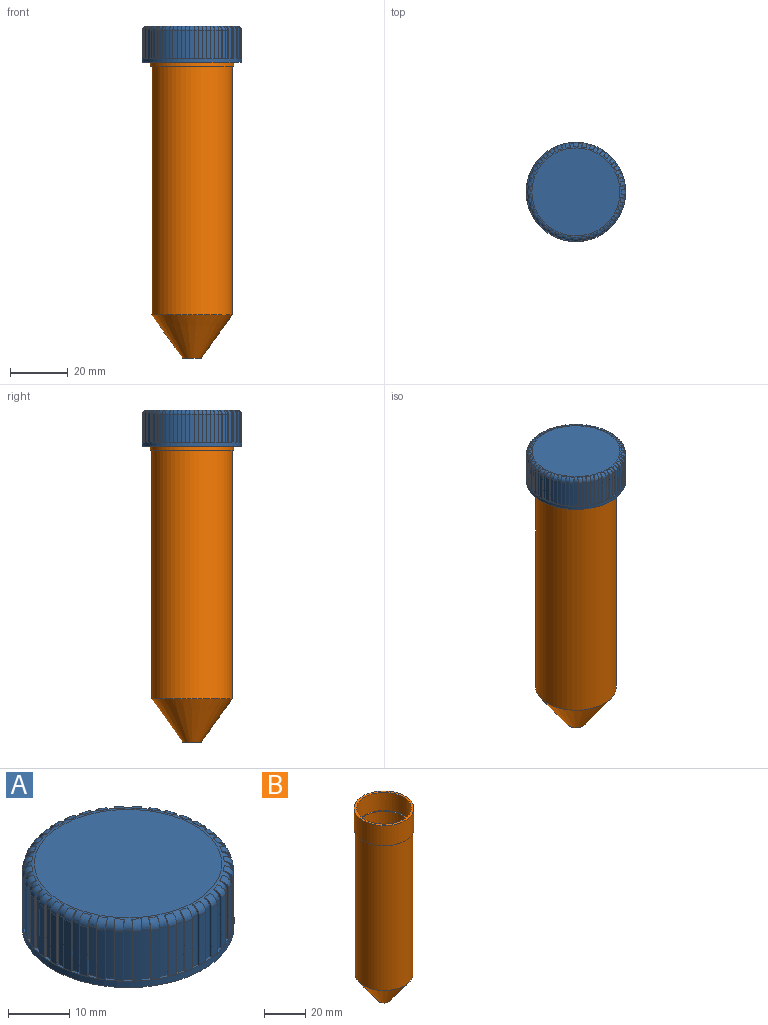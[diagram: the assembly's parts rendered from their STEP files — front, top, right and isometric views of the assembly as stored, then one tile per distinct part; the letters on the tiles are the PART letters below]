
ASSEMBLY  parts=2 mates=1
PART A: 223 faces, bbox 36.3x36.3x12.5 mm
  f0: cylinder r=16.75mm len=9.75mm, axis (0,0,1), area 13.9mm2, adj f37,f42,f179,f184
  f1: cylinder r=16.75mm len=9.75mm, axis (0,0,1), area 13.9mm2, adj f37,f42,f175,f180
  f2: cylinder r=16.75mm len=9.75mm, axis (0,0,1), area 13.9mm2, adj f37,f42,f171,f176
  f3: cylinder r=16.75mm len=9.75mm, axis (0,0,1), area 13.9mm2, adj f37,f42,f167,f172
  f4: cylinder r=16.75mm len=9.75mm, axis (0,0,1), area 13.9mm2, adj f37,f42,f163,f168
  f5: cylinder r=16.75mm len=9.75mm, axis (0,0,1), area 13.9mm2, adj f37,f42,f159,f164
  f6: cylinder r=16.75mm len=9.75mm, axis (0,0,1), area 13.9mm2, adj f37,f42,f155,f160
  f7: cylinder r=16.75mm len=9.75mm, axis (0,0,1), area 13.9mm2, adj f37,f42,f151,f156
  f8: cylinder r=16.75mm len=9.75mm, axis (0,0,1), area 13.9mm2, adj f37,f42,f147,f152
  f9: cylinder r=16.75mm len=9.75mm, axis (0,0,1), area 13.9mm2, adj f37,f42,f143,f148
  f10: cylinder r=16.75mm len=9.75mm, axis (0,0,1), area 13.9mm2, adj f37,f42,f139,f144
  f11: cylinder r=16.75mm len=9.75mm, axis (0,0,1), area 13.9mm2, adj f37,f42,f135,f140
  f12: cylinder r=16.75mm len=9.75mm, axis (0,0,1), area 13.9mm2, adj f37,f42,f131,f136
  f13: cylinder r=16.75mm len=9.75mm, axis (0,0,1), area 13.9mm2, adj f37,f42,f127,f132
  f14: cylinder r=16.75mm len=9.75mm, axis (0,0,1), area 13.9mm2, adj f37,f42,f123,f128
  f15: cylinder r=16.75mm len=9.75mm, axis (0,0,1), area 13.9mm2, adj f37,f42,f119,f124
  f16: cylinder r=16.75mm len=9.75mm, axis (0,0,1), area 13.9mm2, adj f37,f42,f115,f120
  f17: cylinder r=16.75mm len=9.75mm, axis (0,0,1), area 13.9mm2, adj f37,f42,f111,f116
  f18: cylinder r=16.75mm len=9.75mm, axis (0,0,1), area 13.9mm2, adj f37,f42,f107,f112
  f19: cylinder r=16.75mm len=9.75mm, axis (0,0,1), area 13.9mm2, adj f37,f42,f103,f108
  f20: cylinder r=16.75mm len=9.75mm, axis (0,0,1), area 13.9mm2, adj f37,f42,f99,f104
  f21: cylinder r=16.75mm len=9.75mm, axis (0,0,1), area 13.9mm2, adj f37,f42,f95,f100
  f22: cylinder r=16.75mm len=9.75mm, axis (0,0,1), area 13.9mm2, adj f37,f42,f91,f96
  f23: cylinder r=16.75mm len=9.75mm, axis (0,0,1), area 13.9mm2, adj f37,f42,f87,f92
  f24: cylinder r=16.75mm len=9.75mm, axis (0,0,1), area 13.9mm2, adj f37,f42,f83,f88
  f25: cylinder r=16.75mm len=9.75mm, axis (0,0,1), area 13.9mm2, adj f37,f42,f79,f84
  f26: cylinder r=16.75mm len=9.75mm, axis (0,0,1), area 13.9mm2, adj f37,f42,f75,f80
  f27: cylinder r=16.75mm len=9.75mm, axis (0,0,1), area 13.9mm2, adj f37,f42,f71,f76
  f28: cylinder r=16.75mm len=9.75mm, axis (0,0,1), area 13.9mm2, adj f37,f42,f67,f72
  f29: cylinder r=16.75mm len=9.75mm, axis (0,0,1), area 13.9mm2, adj f37,f42,f63,f68
  f30: cylinder r=16.75mm len=9.75mm, axis (0,0,1), area 13.9mm2, adj f37,f42,f59,f64
  f31: cylinder r=16.75mm len=9.75mm, axis (0,0,1), area 13.9mm2, adj f37,f42,f55,f60
  f32: cylinder r=16.75mm len=9.75mm, axis (0,0,1), area 13.9mm2, adj f37,f42,f51,f56
  f33: cylinder r=16.75mm len=9.75mm, axis (0,0,1), area 13.9mm2, adj f37,f42,f47,f52
  f34: cylinder r=16.75mm len=9.75mm, axis (0,0,1), area 13.9mm2, adj f37,f42,f43,f48
  f35: plane 30.5x30.5mm, normal (0,0,1), area 730.6mm2, adj f42
  f36: cylinder r=16.75mm len=9.75mm, axis (0,0,1), area 13.9mm2, adj f37,f42,f44,f183
  f37: plane 34.5x34.5mm, normal (0,0,1), area 31.5mm2, adj f0,f1,f2,f3,f4,f5,f6,f7
  f38: cylinder r=17.25mm len=34.5mm, axis (0,0,1), area 135.5mm2, adj f37,f39
  f39: plane 34.5x34.5mm, normal (0,0,-1), area 175.2mm2, adj f38,f40
  f40: cylinder r=15.55mm len=31.1mm, axis (0,0,1), area 1025.9mm2, adj f39,f41
  f41: plane 31.1x31.1mm, normal (0,0,-1), area 759.6mm2, adj f40
  f42: torus R=15.25mm, axis (0,0,-1), area 134.8mm2, adj f0,f1,f2,f3,f4,f5,f6,f7
  f43: plane 11.25x1.5mm, normal (0,1,0), area 4.7mm2, adj f34,f37,f42,f45,f46,f222
  f44: plane 11.25x1.5mm, normal (0,-1,0), area 4.7mm2, adj f36,f37,f42,f45,f46,f222
  f45: plane 9.75x1.5mm, normal (-1,0,0), area 14.6mm2, adj f37,f43,f44,f222
  f46: plane 1.51x0.07mm, normal (1,0,0), area 0.1mm2, adj f42,f43,f44,f222
  f47: plane 11.25x1.48mm, normal (0.17,0.98,0), area 4.7mm2, adj f33,f37,f42,f49,f50,f221
  f48: plane 11.25x1.48mm, normal (-0.17,-0.98,0), area 4.7mm2, adj f34,f37,f42,f49,f50,f221
  f49: plane 9.75x1.48mm, normal (-0.98,0.17,0), area 14.6mm2, adj f37,f47,f48,f221
  f50: plane 1.48x0.26mm, normal (0.98,-0.17,0), area 0.1mm2, adj f42,f47,f48,f221
  f51: plane 11.25x1.41mm, normal (0.34,0.94,0), area 4.7mm2, adj f32,f37,f42,f53,f54,f220
  f52: plane 11.25x1.41mm, normal (-0.34,-0.94,0), area 4.7mm2, adj f33,f37,f42,f53,f54,f220
  f53: plane 9.75x1.41mm, normal (-0.94,0.34,0), area 14.6mm2, adj f37,f51,f52,f220
  f54: plane 1.41x0.51mm, normal (0.94,-0.34,0), area 0.1mm2, adj f42,f51,f52,f220
  f55: plane 11.25x1.3mm, normal (0.5,0.87,0), area 4.7mm2, adj f31,f37,f42,f57,f58,f219
  f56: plane 11.25x1.3mm, normal (-0.5,-0.87,0), area 4.7mm2, adj f32,f37,f42,f57,f58,f219
  f57: plane 9.75x1.3mm, normal (-0.87,0.5,0), area 14.6mm2, adj f37,f55,f56,f219
  f58: plane 1.3x0.75mm, normal (0.87,-0.5,0), area 0.1mm2, adj f42,f55,f56,f219
  f59: plane 11.25x1.15mm, normal (0.64,0.77,0), area 4.7mm2, adj f30,f37,f42,f61,f62,f218
  f60: plane 11.25x1.15mm, normal (-0.64,-0.77,0), area 4.7mm2, adj f31,f37,f42,f61,f62,f218
  f61: plane 9.75x1.15mm, normal (-0.77,0.64,0), area 14.6mm2, adj f37,f59,f60,f218
  f62: plane 1.15x0.96mm, normal (0.77,-0.64,0), area 0.1mm2, adj f42,f59,f60,f218
  f63: plane 11.25x1.15mm, normal (0.77,0.64,0), area 4.7mm2, adj f29,f37,f42,f65,f66,f217
  f64: plane 11.25x1.15mm, normal (-0.77,-0.64,0), area 4.7mm2, adj f30,f37,f42,f65,f66,f217
  f65: plane 9.75x1.15mm, normal (-0.64,0.77,0), area 14.6mm2, adj f37,f63,f64,f217
  f66: plane 1.15x0.96mm, normal (0.64,-0.77,0), area 0.1mm2, adj f42,f63,f64,f217
  f67: plane 11.25x1.3mm, normal (0.87,0.5,0), area 4.7mm2, adj f28,f37,f42,f69,f70,f216
  f68: plane 11.25x1.3mm, normal (-0.87,-0.5,0), area 4.7mm2, adj f29,f37,f42,f69,f70,f216
  f69: plane 9.75x1.3mm, normal (-0.5,0.87,0), area 14.6mm2, adj f37,f67,f68,f216
  f70: plane 1.3x0.75mm, normal (0.5,-0.87,0), area 0.1mm2, adj f42,f67,f68,f216
  f71: plane 11.25x1.41mm, normal (0.94,0.34,0), area 4.7mm2, adj f27,f37,f42,f73,f74,f215
  f72: plane 11.25x1.41mm, normal (-0.94,-0.34,0), area 4.7mm2, adj f28,f37,f42,f73,f74,f215
  f73: plane 9.75x1.41mm, normal (-0.34,0.94,0), area 14.6mm2, adj f37,f71,f72,f215
  f74: plane 1.41x0.51mm, normal (0.34,-0.94,0), area 0.1mm2, adj f42,f71,f72,f215
  f75: plane 11.25x1.48mm, normal (0.98,0.17,0), area 4.7mm2, adj f26,f37,f42,f77,f78,f214
  f76: plane 11.25x1.48mm, normal (-0.98,-0.17,0), area 4.7mm2, adj f27,f37,f42,f77,f78,f214
  f77: plane 9.75x1.48mm, normal (-0.17,0.98,0), area 14.6mm2, adj f37,f75,f76,f214
  f78: plane 1.48x0.26mm, normal (0.17,-0.98,0), area 0.1mm2, adj f42,f75,f76,f214
  f79: plane 11.25x1.5mm, normal (1,0,0), area 4.7mm2, adj f25,f37,f42,f81,f82,f213
  f80: plane 11.25x1.5mm, normal (-1,0,0), area 4.7mm2, adj f26,f37,f42,f81,f82,f213
  f81: plane 9.75x1.5mm, normal (0,1,0), area 14.6mm2, adj f37,f79,f80,f213
  f82: plane 1.5x0.06mm, normal (0,-1,0), area 0.1mm2, adj f42,f79,f80,f213
  f83: plane 11.25x1.48mm, normal (0.98,-0.17,0), area 4.7mm2, adj f24,f37,f42,f85,f86,f212
  f84: plane 11.25x1.48mm, normal (-0.98,0.17,0), area 4.7mm2, adj f25,f37,f42,f85,f86,f212
  f85: plane 9.75x1.48mm, normal (0.17,0.98,0), area 14.6mm2, adj f37,f83,f84,f212
  f86: plane 1.48x0.26mm, normal (-0.17,-0.98,0), area 0.1mm2, adj f42,f83,f84,f212
  f87: plane 11.25x1.41mm, normal (0.94,-0.34,0), area 4.7mm2, adj f23,f37,f42,f89,f90,f211
  f88: plane 11.25x1.41mm, normal (-0.94,0.34,0), area 4.7mm2, adj f24,f37,f42,f89,f90,f211
  f89: plane 9.75x1.41mm, normal (0.34,0.94,0), area 14.6mm2, adj f37,f87,f88,f211
  f90: plane 1.41x0.51mm, normal (-0.34,-0.94,0), area 0.1mm2, adj f42,f87,f88,f211
  f91: plane 11.25x1.3mm, normal (0.87,-0.5,0), area 4.7mm2, adj f22,f37,f42,f93,f94,f210
  f92: plane 11.25x1.3mm, normal (-0.87,0.5,0), area 4.7mm2, adj f23,f37,f42,f93,f94,f210
  f93: plane 9.75x1.3mm, normal (0.5,0.87,0), area 14.6mm2, adj f37,f91,f92,f210
  f94: plane 1.3x0.75mm, normal (-0.5,-0.87,0), area 0.1mm2, adj f42,f91,f92,f210
  f95: plane 11.25x1.15mm, normal (0.77,-0.64,0), area 4.7mm2, adj f21,f37,f42,f97,f98,f209
  f96: plane 11.25x1.15mm, normal (-0.77,0.64,0), area 4.7mm2, adj f22,f37,f42,f97,f98,f209
  f97: plane 9.75x1.15mm, normal (0.64,0.77,0), area 14.6mm2, adj f37,f95,f96,f209
  f98: plane 1.15x0.96mm, normal (-0.64,-0.77,0), area 0.1mm2, adj f42,f95,f96,f209
  f99: plane 11.25x1.15mm, normal (0.64,-0.77,0), area 4.7mm2, adj f20,f37,f42,f101,f102,f208
  f100: plane 11.25x1.15mm, normal (-0.64,0.77,0), area 4.7mm2, adj f21,f37,f42,f101,f102,f208
  f101: plane 9.75x1.15mm, normal (0.77,0.64,0), area 14.6mm2, adj f37,f99,f100,f208
  f102: plane 1.15x0.96mm, normal (-0.77,-0.64,0), area 0.1mm2, adj f42,f99,f100,f208
  f103: plane 11.25x1.3mm, normal (0.5,-0.87,0), area 4.7mm2, adj f19,f37,f42,f105,f106,f207
  f104: plane 11.25x1.3mm, normal (-0.5,0.87,0), area 4.7mm2, adj f20,f37,f42,f105,f106,f207
  f105: plane 9.75x1.3mm, normal (0.87,0.5,0), area 14.6mm2, adj f37,f103,f104,f207
  f106: plane 1.3x0.75mm, normal (-0.87,-0.5,0), area 0.1mm2, adj f42,f103,f104,f207
  f107: plane 11.25x1.41mm, normal (0.34,-0.94,0), area 4.7mm2, adj f18,f37,f42,f109,f110,f206
  f108: plane 11.25x1.41mm, normal (-0.34,0.94,0), area 4.7mm2, adj f19,f37,f42,f109,f110,f206
  f109: plane 9.75x1.41mm, normal (0.94,0.34,0), area 14.6mm2, adj f37,f107,f108,f206
  f110: plane 1.41x0.51mm, normal (-0.94,-0.34,0), area 0.1mm2, adj f42,f107,f108,f206
  f111: plane 11.25x1.48mm, normal (0.17,-0.98,0), area 4.7mm2, adj f17,f37,f42,f113,f114,f205
  f112: plane 11.25x1.48mm, normal (-0.17,0.98,0), area 4.7mm2, adj f18,f37,f42,f113,f114,f205
  f113: plane 9.75x1.48mm, normal (0.98,0.17,0), area 14.6mm2, adj f37,f111,f112,f205
  f114: plane 1.48x0.26mm, normal (-0.98,-0.17,0), area 0.1mm2, adj f42,f111,f112,f205
  f115: plane 11.25x1.5mm, normal (0,-1,0), area 4.7mm2, adj f16,f37,f42,f117,f118,f204
  f116: plane 11.25x1.5mm, normal (0,1,0), area 4.7mm2, adj f17,f37,f42,f117,f118,f204
  f117: plane 9.75x1.5mm, normal (1,0,0), area 14.6mm2, adj f37,f115,f116,f204
  f118: plane 1.5x0.06mm, normal (-1,0,0), area 0.1mm2, adj f42,f115,f116,f204
  f119: plane 11.25x1.48mm, normal (-0.17,-0.98,0), area 4.7mm2, adj f15,f37,f42,f121,f122,f203
  f120: plane 11.25x1.48mm, normal (0.17,0.98,0), area 4.7mm2, adj f16,f37,f42,f121,f122,f203
  f121: plane 9.75x1.48mm, normal (0.98,-0.17,0), area 14.6mm2, adj f37,f119,f120,f203
  f122: plane 1.48x0.26mm, normal (-0.98,0.17,0), area 0.1mm2, adj f42,f119,f120,f203
  f123: plane 11.25x1.41mm, normal (-0.34,-0.94,0), area 4.7mm2, adj f14,f37,f42,f125,f126,f202
  f124: plane 11.25x1.41mm, normal (0.34,0.94,0), area 4.7mm2, adj f15,f37,f42,f125,f126,f202
  f125: plane 9.75x1.41mm, normal (0.94,-0.34,0), area 14.6mm2, adj f37,f123,f124,f202
  f126: plane 1.41x0.51mm, normal (-0.94,0.34,0), area 0.1mm2, adj f42,f123,f124,f202
  f127: plane 11.25x1.3mm, normal (-0.5,-0.87,0), area 4.7mm2, adj f13,f37,f42,f129,f130,f201
  f128: plane 11.25x1.3mm, normal (0.5,0.87,0), area 4.7mm2, adj f14,f37,f42,f129,f130,f201
  f129: plane 9.75x1.3mm, normal (0.87,-0.5,0), area 14.6mm2, adj f37,f127,f128,f201
  f130: plane 1.3x0.75mm, normal (-0.87,0.5,0), area 0.1mm2, adj f42,f127,f128,f201
  f131: plane 11.25x1.15mm, normal (-0.64,-0.77,0), area 4.7mm2, adj f12,f37,f42,f133,f134,f200
  f132: plane 11.25x1.15mm, normal (0.64,0.77,0), area 4.7mm2, adj f13,f37,f42,f133,f134,f200
  f133: plane 9.75x1.15mm, normal (0.77,-0.64,0), area 14.6mm2, adj f37,f131,f132,f200
  f134: plane 1.15x0.96mm, normal (-0.77,0.64,0), area 0.1mm2, adj f42,f131,f132,f200
  f135: plane 11.25x1.15mm, normal (-0.77,-0.64,0), area 4.7mm2, adj f11,f37,f42,f137,f138,f199
  f136: plane 11.25x1.15mm, normal (0.77,0.64,0), area 4.7mm2, adj f12,f37,f42,f137,f138,f199
  f137: plane 9.75x1.15mm, normal (0.64,-0.77,0), area 14.6mm2, adj f37,f135,f136,f199
  f138: plane 1.15x0.96mm, normal (-0.64,0.77,0), area 0.1mm2, adj f42,f135,f136,f199
  f139: plane 11.25x1.3mm, normal (-0.87,-0.5,0), area 4.7mm2, adj f10,f37,f42,f141,f142,f198
  f140: plane 11.25x1.3mm, normal (0.87,0.5,0), area 4.7mm2, adj f11,f37,f42,f141,f142,f198
  f141: plane 9.75x1.3mm, normal (0.5,-0.87,0), area 14.6mm2, adj f37,f139,f140,f198
  f142: plane 1.3x0.75mm, normal (-0.5,0.87,0), area 0.1mm2, adj f42,f139,f140,f198
  f143: plane 11.25x1.41mm, normal (-0.94,-0.34,0), area 4.7mm2, adj f9,f37,f42,f145,f146,f197
  f144: plane 11.25x1.41mm, normal (0.94,0.34,0), area 4.7mm2, adj f10,f37,f42,f145,f146,f197
  f145: plane 9.75x1.41mm, normal (0.34,-0.94,0), area 14.6mm2, adj f37,f143,f144,f197
  f146: plane 1.41x0.51mm, normal (-0.34,0.94,0), area 0.1mm2, adj f42,f143,f144,f197
  f147: plane 11.25x1.48mm, normal (-0.98,-0.17,0), area 4.7mm2, adj f8,f37,f42,f149,f150,f196
  f148: plane 11.25x1.48mm, normal (0.98,0.17,0), area 4.7mm2, adj f9,f37,f42,f149,f150,f196
  f149: plane 9.75x1.48mm, normal (0.17,-0.98,0), area 14.6mm2, adj f37,f147,f148,f196
  f150: plane 1.48x0.26mm, normal (-0.17,0.98,0), area 0.1mm2, adj f42,f147,f148,f196
  f151: plane 11.25x1.5mm, normal (-1,0,0), area 4.7mm2, adj f7,f37,f42,f153,f154,f195
  f152: plane 11.25x1.5mm, normal (1,0,0), area 4.7mm2, adj f8,f37,f42,f153,f154,f195
  f153: plane 9.75x1.5mm, normal (0,-1,0), area 14.6mm2, adj f37,f151,f152,f195
  f154: plane 1.5x0.06mm, normal (0,1,0), area 0.1mm2, adj f42,f151,f152,f195
  f155: plane 11.25x1.48mm, normal (-0.98,0.17,0), area 4.7mm2, adj f6,f37,f42,f157,f158,f194
  f156: plane 11.25x1.48mm, normal (0.98,-0.17,0), area 4.7mm2, adj f7,f37,f42,f157,f158,f194
  f157: plane 9.75x1.48mm, normal (-0.17,-0.98,0), area 14.6mm2, adj f37,f155,f156,f194
  f158: plane 1.48x0.26mm, normal (0.17,0.98,0), area 0.1mm2, adj f42,f155,f156,f194
  f159: plane 11.25x1.41mm, normal (-0.94,0.34,0), area 4.7mm2, adj f5,f37,f42,f161,f162,f193
  f160: plane 11.25x1.41mm, normal (0.94,-0.34,0), area 4.7mm2, adj f6,f37,f42,f161,f162,f193
  f161: plane 9.75x1.41mm, normal (-0.34,-0.94,0), area 14.6mm2, adj f37,f159,f160,f193
  f162: plane 1.41x0.51mm, normal (0.34,0.94,0), area 0.1mm2, adj f42,f159,f160,f193
  f163: plane 11.25x1.3mm, normal (-0.87,0.5,0), area 4.7mm2, adj f4,f37,f42,f165,f166,f192
  f164: plane 11.25x1.3mm, normal (0.87,-0.5,0), area 4.7mm2, adj f5,f37,f42,f165,f166,f192
  f165: plane 9.75x1.3mm, normal (-0.5,-0.87,0), area 14.6mm2, adj f37,f163,f164,f192
  f166: plane 1.3x0.75mm, normal (0.5,0.87,0), area 0.1mm2, adj f42,f163,f164,f192
  f167: plane 11.25x1.15mm, normal (-0.77,0.64,0), area 4.7mm2, adj f3,f37,f42,f169,f170,f191
  f168: plane 11.25x1.15mm, normal (0.77,-0.64,0), area 4.7mm2, adj f4,f37,f42,f169,f170,f191
  f169: plane 9.75x1.15mm, normal (-0.64,-0.77,0), area 14.6mm2, adj f37,f167,f168,f191
  f170: plane 1.15x0.96mm, normal (0.64,0.77,0), area 0.1mm2, adj f42,f167,f168,f191
  f171: plane 11.25x1.15mm, normal (-0.64,0.77,0), area 4.7mm2, adj f2,f37,f42,f173,f174,f190
  f172: plane 11.25x1.15mm, normal (0.64,-0.77,0), area 4.7mm2, adj f3,f37,f42,f173,f174,f190
  f173: plane 9.75x1.15mm, normal (-0.77,-0.64,0), area 14.6mm2, adj f37,f171,f172,f190
  f174: plane 1.15x0.96mm, normal (0.77,0.64,0), area 0.1mm2, adj f42,f171,f172,f190
  f175: plane 11.25x1.3mm, normal (-0.5,0.87,0), area 4.7mm2, adj f1,f37,f42,f177,f178,f189
  f176: plane 11.25x1.3mm, normal (0.5,-0.87,0), area 4.7mm2, adj f2,f37,f42,f177,f178,f189
  f177: plane 9.75x1.3mm, normal (-0.87,-0.5,0), area 14.6mm2, adj f37,f175,f176,f189
  f178: plane 1.3x0.75mm, normal (0.87,0.5,0), area 0.1mm2, adj f42,f175,f176,f189
  f179: plane 11.25x1.41mm, normal (-0.34,0.94,0), area 4.7mm2, adj f0,f37,f42,f181,f182,f188
  f180: plane 11.25x1.41mm, normal (0.34,-0.94,0), area 4.7mm2, adj f1,f37,f42,f181,f182,f188
  f181: plane 9.75x1.41mm, normal (-0.94,-0.34,0), area 14.6mm2, adj f37,f179,f180,f188
  f182: plane 1.41x0.51mm, normal (0.94,0.34,0), area 0.1mm2, adj f42,f179,f180,f188
  f183: plane 11.25x1.48mm, normal (-0.17,0.98,0), area 4.7mm2, adj f36,f37,f42,f185,f186,f187
  f184: plane 11.25x1.48mm, normal (0.17,-0.98,0), area 4.7mm2, adj f0,f37,f42,f185,f186,f187
  f185: plane 9.75x1.48mm, normal (-0.98,-0.17,0), area 14.6mm2, adj f37,f183,f184,f187
  f186: plane 1.48x0.26mm, normal (0.98,0.17,0), area 0.1mm2, adj f42,f183,f184,f187
  f187: cylinder r=1.5mm len=1.74mm, axis (-0.17,0.98,0), area 3.5mm2, adj f183,f184,f185,f186
  f188: cylinder r=1.5mm len=1.92mm, axis (-0.34,0.94,0), area 3.5mm2, adj f179,f180,f181,f182
  f189: cylinder r=1.5mm len=2.05mm, axis (-0.5,0.87,0), area 3.5mm2, adj f175,f176,f177,f178
  f190: cylinder r=1.5mm len=2.11mm, axis (-0.64,0.77,0), area 3.5mm2, adj f171,f172,f173,f174
  f191: cylinder r=1.5mm len=2.11mm, axis (-0.77,0.64,0), area 3.5mm2, adj f167,f168,f169,f170
  f192: cylinder r=1.5mm len=2.05mm, axis (-0.87,0.5,0), area 3.5mm2, adj f163,f164,f165,f166
  f193: cylinder r=1.5mm len=1.92mm, axis (-0.94,0.34,0), area 3.5mm2, adj f159,f160,f161,f162
  f194: cylinder r=1.5mm len=1.74mm, axis (-0.98,0.17,0), area 3.5mm2, adj f155,f156,f157,f158
  f195: cylinder r=1.5mm len=1.5mm, axis (-1,0,0), area 3.5mm2, adj f151,f152,f153,f154
  f196: cylinder r=1.5mm len=1.74mm, axis (-0.98,-0.17,0), area 3.5mm2, adj f147,f148,f149,f150
  f197: cylinder r=1.5mm len=1.92mm, axis (-0.94,-0.34,0), area 3.5mm2, adj f143,f144,f145,f146
  f198: cylinder r=1.5mm len=2.05mm, axis (-0.87,-0.5,0), area 3.5mm2, adj f139,f140,f141,f142
  f199: cylinder r=1.5mm len=2.11mm, axis (-0.77,-0.64,0), area 3.5mm2, adj f135,f136,f137,f138
  f200: cylinder r=1.5mm len=2.11mm, axis (-0.64,-0.77,0), area 3.5mm2, adj f131,f132,f133,f134
  f201: cylinder r=1.5mm len=2.05mm, axis (-0.5,-0.87,0), area 3.5mm2, adj f127,f128,f129,f130
  f202: cylinder r=1.5mm len=1.92mm, axis (-0.34,-0.94,0), area 3.5mm2, adj f123,f124,f125,f126
  f203: cylinder r=1.5mm len=1.74mm, axis (-0.17,-0.98,0), area 3.5mm2, adj f119,f120,f121,f122
  f204: cylinder r=1.5mm len=1.5mm, axis (0,-1,0), area 3.5mm2, adj f115,f116,f117,f118
  f205: cylinder r=1.5mm len=1.74mm, axis (0.17,-0.98,0), area 3.5mm2, adj f111,f112,f113,f114
  f206: cylinder r=1.5mm len=1.92mm, axis (0.34,-0.94,0), area 3.5mm2, adj f107,f108,f109,f110
  f207: cylinder r=1.5mm len=2.05mm, axis (0.5,-0.87,0), area 3.5mm2, adj f103,f104,f105,f106
  f208: cylinder r=1.5mm len=2.11mm, axis (0.64,-0.77,0), area 3.5mm2, adj f99,f100,f101,f102
  f209: cylinder r=1.5mm len=2.11mm, axis (0.77,-0.64,0), area 3.5mm2, adj f95,f96,f97,f98
  f210: cylinder r=1.5mm len=2.05mm, axis (0.87,-0.5,0), area 3.5mm2, adj f91,f92,f93,f94
  f211: cylinder r=1.5mm len=1.92mm, axis (0.94,-0.34,0), area 3.5mm2, adj f87,f88,f89,f90
  f212: cylinder r=1.5mm len=1.74mm, axis (0.98,-0.17,0), area 3.5mm2, adj f83,f84,f85,f86
  f213: cylinder r=1.5mm len=1.5mm, axis (1,0,0), area 3.5mm2, adj f79,f80,f81,f82
  f214: cylinder r=1.5mm len=1.74mm, axis (0.98,0.17,0), area 3.5mm2, adj f75,f76,f77,f78
  f215: cylinder r=1.5mm len=1.92mm, axis (0.94,0.34,0), area 3.5mm2, adj f71,f72,f73,f74
  f216: cylinder r=1.5mm len=2.05mm, axis (0.87,0.5,0), area 3.5mm2, adj f67,f68,f69,f70
  f217: cylinder r=1.5mm len=2.11mm, axis (0.77,0.64,0), area 3.5mm2, adj f63,f64,f65,f66
  f218: cylinder r=1.5mm len=2.11mm, axis (0.64,0.77,0), area 3.5mm2, adj f59,f60,f61,f62
  f219: cylinder r=1.5mm len=2.05mm, axis (0.5,0.87,0), area 3.5mm2, adj f55,f56,f57,f58
  f220: cylinder r=1.5mm len=1.92mm, axis (0.34,0.94,0), area 3.5mm2, adj f51,f52,f53,f54
  f221: cylinder r=1.5mm len=1.74mm, axis (0.17,0.98,0), area 3.5mm2, adj f47,f48,f49,f50
  f222: cylinder r=1.5mm len=1.5mm, axis (0,1,0), area 3.5mm2, adj f43,f44,f45,f46
PART B: 11 faces, bbox 29x29x113 mm
  f0: plane 29x29mm, normal (0,0,1), area 109mm2, adj f1,f6
  f1: cylinder r=14.5mm len=29mm, axis (0,0,1), area 1093.3mm2, adj f0,f2
  f2: plane 29x29mm, normal (0,0,-1), area 44.8mm2, adj f1,f3
  f3: cylinder r=14mm len=86mm, axis (0,0,1), area 7565mm2, adj f2,f4
  f4: cone r=3.25mm half-angle=35.6deg, axis (0,0,1), area 1000.1mm2, adj f3,f5
  f5: plane 6.5x6.5mm, normal (0,0,-1), area 33.2mm2, adj f4
  f6: cylinder r=13.25mm len=26.5mm, axis (0,0,1), area 895mm2, adj f0,f7
  f7: plane 26.5x26.5mm, normal (0,0,1), area 40.8mm2, adj f6,f8
  f8: cylinder r=12.75mm len=86.85mm, axis (0,0,1), area 6957.5mm2, adj f7,f9
  f9: cone r=2.23mm half-angle=35.6deg, axis (0,0,1), area 840mm2, adj f8,f10
  f10: plane 5.22x5.22mm, normal (0,0,1), area 21.4mm2, adj f9
PLACE A t=(-47.09,-2.96,82.34)mm
PLACE B t=(-47.09,-2.96,-20.16)mm
MATE revolute A.f0 <-> B.f1  axis (0,0,-1) through (-47.09,-2.96,92.84)mm
